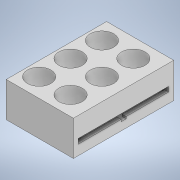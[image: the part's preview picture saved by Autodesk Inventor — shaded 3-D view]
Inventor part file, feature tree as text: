
AUTODESK INVENTOR PART (.ipt)
format: ipt  version: 2020 (Build 240168000, 168)  size: 251,904 bytes
history: native  units: in
note: dims shown in document units (in); Inventor stores cm internally (conversion verified against a paired STEP export)
features: extrude x6, sketch x6, pattern_linear x1
ambient origin geometry x8: Origin, YZ Plane, XZ Plane, XY Plane, X Axis, Y Axis, Z Axis, Center Point
bodies: Solid1 (feature_tree)
feature tree (13):
  extrude  "Extrusion1"  Depth=5.0299in
  extrude  "Extrusion2"  Depth=0.375in
  extrude  "Extrusion3"  Depth=0.5in
  sketch  "Sketch5"  dims[d24=5.315in d25=4.5472in]
  extrude  "Extrusion16"  Depth=4.5472in
  extrude  "Extrusion17"  Depth=0.25in
  extrude  "Extrusion18"  Depth=0.75in
  pattern_linear  "Rectangular Pattern2"  Spacing1=1.05in  [1 undecoded]
  sketch  "Sketch1"  dims[d0=3.3654in d1=5.0299in]
  sketch  "Sketch3"  dims[d3=45.0deg d4=0.375in]
  sketch  "Sketch4"  dims[d5=0.5in d6=0.0in d23=2.8543in]
  sketch  "Sketch22"  dims[d26=0.1in d27=0.0in d28=0.25in]
  sketch  "Sketch23"  dims[d29=0.1in d30=0.0in d31=2.6575in d32=1.05in d33=1.25in d154=0.25in d155=0.0in d156=1.0in d157=0.0in d158=1.1787in d159=1.5in d160=0.0in d161=1.1811in d163=1.5748in d164=0.7874in d166=1.5748in d45=1.0in d46=1.0in d47=1.0in d48=0.15in d49=0.201in d50=0.375in d51=0.5635in d52=0.75in d53=0.8108in d54=0.0625in d55=0.75in d56=0.375in]
note: 1 required parameter value undecoded (feature->parameter linkage not recoverable at this tier; creation-order binding heuristic only, values carry confidence <= 0.55)
